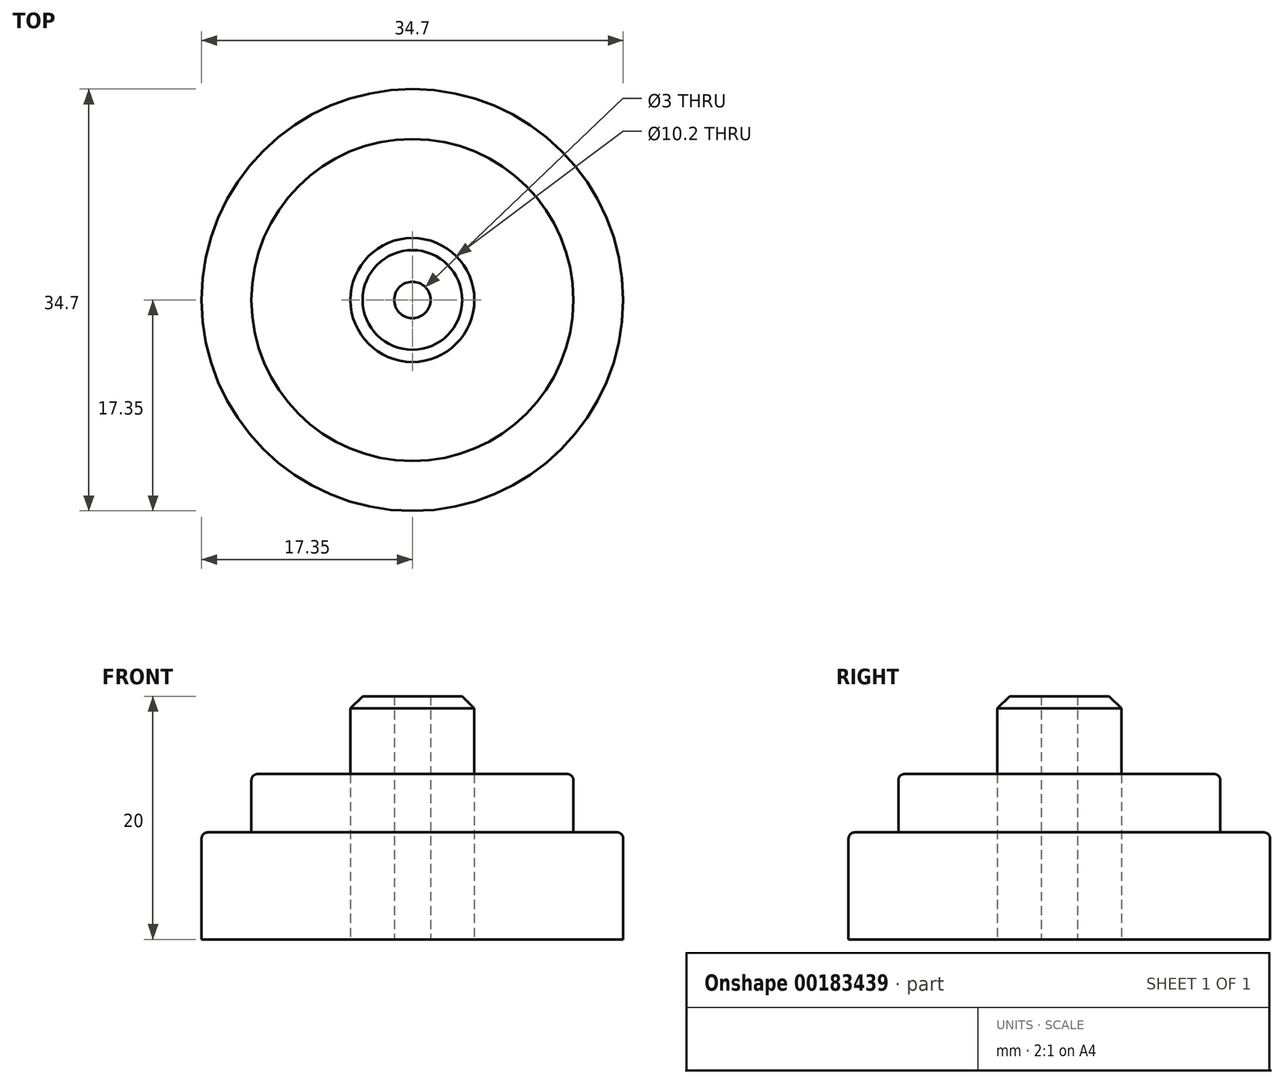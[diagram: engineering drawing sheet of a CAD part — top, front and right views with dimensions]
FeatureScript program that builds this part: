
annotation { "Feature Type Name" : "Feature", "Feature Type Description" : "" }
export const myFeature = defineFeature(function(context is Context, id is Id, definition is map)
    precondition{}
    {
        {
            var Q0;
            Q0=qCreatedBy(makeId("Top.planeOp"),FACE);
            var sketch = newSketch(context, id + "F0", { "sketchPlane" : qUnion([Q0])});
            skCircle(sketch, "E0", {"center": v(0, 0) * mm, "radius": 13.25 * mm});
            skCircle(sketch, "E1", {"center": v(0, 0) * mm, "radius": 17.35 * mm});
            skCircle(sketch, "E2", {"center": v(0, 0) * mm, "radius": 5.1 * mm});
            skCircle(sketch, "E3", {"center": v(0, 0) * mm, "radius": 1.5 * mm});
            skSolve(sketch);
        }
        {
            var Q0;
            Q0=makeQuery(id+"F0.imprint","IMPRINT",FACE,{"disambiguationData":[TD([[makeQuery(id+"F0.imprint","IMPRINT",EDGE,{"derivedFrom":sQuery(id+"F0.wireOp",EDGE,"E0")}),-1.0]])]});
            extrude(context, id + "F1", {"entities" : qUnion([Q0]), "depth" : 8.8 * mm});
        }
        {
            var Q0;
            Q0=makeQuery(id+"F0.imprint","IMPRINT",FACE,{"disambiguationData":[TD([[makeQuery(id+"F0.imprint","IMPRINT",EDGE,{"derivedFrom":sQuery(id+"F0.wireOp",EDGE,"E0")}),1.0]])]});
            extrude(context, id + "F2", {"entities" : qUnion([Q0]), "operationType" : NewBodyOperationType.ADD, "depth" : 13.6 * mm});
        }
        {
            var Q0;
            Q0=makeQuery(id+"F0.imprint","IMPRINT",FACE,{"disambiguationData":[TD([[makeQuery(id+"F0.imprint","IMPRINT",EDGE,{"derivedFrom":sQuery(id+"F0.wireOp",EDGE,"E2")}),1.0]])]});
            extrude(context, id + "F3", {"entities" : qUnion([Q0]), "depth" : 20 * mm});
        }
        {
            var Q0;
            Q0=makeQuery(id+"F2.opExtrude","CAP_EDGE",EDGE,{"disambiguationData":[OSD([sQuery(id+"F0.wireOp",EDGE,"E0")])],"isStart":false});
            fillet(context, id + "F4", {"entities" : qUnion([Q0]), "radius" : 0.5 * mm, "tangentPropagation" : true, "allowEdgeOverflow" : false});
        }
        {
            var Q0;
            Q0=makeQuery(id+"F1.opExtrude","CAP_EDGE",EDGE,{"disambiguationData":[OSD([sQuery(id+"F0.wireOp",EDGE,"E1")])],"isStart":false});
            fillet(context, id + "F5", {"entities" : qUnion([Q0]), "radius" : 0.5 * mm, "tangentPropagation" : true, "allowEdgeOverflow" : false});
        }
        {
            var Q0;
            Q0=makeQuery(id+"F3.opExtrude","CAP_EDGE",EDGE,{"disambiguationData":[OSD([sQuery(id+"F0.wireOp",EDGE,"E2")])],"isStart":false});
            chamfer(context, id + "F6", {"entities" : qUnion([Q0]), "width" : 1 * mm, "tangentPropagation" : true});
        }
    });
